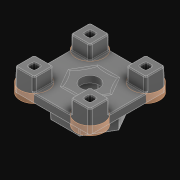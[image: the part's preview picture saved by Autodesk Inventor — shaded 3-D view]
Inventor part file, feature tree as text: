
AUTODESK INVENTOR PART (.ipt)
format: ipt  version: 2021 (Build 250183000, 183)  size: 695,808 bytes
history: native  units: in
note: dims shown in document units (in); Inventor stores cm internally (conversion verified against a paired STEP export)
features: projected_geometry x4, other x4, extrude x4, sketch x2, pattern_linear x1, fillet x1
ambient origin geometry x8: Origin, YZ Plane, XZ Plane, XY Plane, X Axis, Y Axis, Z Axis, Center Point
bodies: Solid1 (feature_tree)
feature tree (16):
  sketch  "Sketch2"  dims[d1=0.25in d2=0.25in d3=0.25in d4=0.0787in d5=0.0in d6=0.25in d7=0.25in d8=0.25in d9=0.25in d24=0.7874in d26=0.5in d27=0.7874in d29=0.5in d30=0.25in d31=0.25in]
  pattern_linear  "Rectangular Pattern1"  Spacing1=0.25in  [1 undecoded]
  sketch  "Sketch1"  dims[d0=0.25in]
  projected_geometry  "Projected Loop1"
  projected_geometry  "Projected Loop2"
  projected_geometry  "Projected Loop3"
  projected_geometry  "Projected Loop4"
  other  "Srf1"
  other  "Srf5"
  other  "Srf6"
  other  "Srf7"
  fillet  "Fillet8"  Radius=0.25in
  extrude  "ExtrusionSrf1"  Depth=0.0787in TaperAngle=0.0deg
  extrude  "ExtrusionSrf5"  Depth=0.25in
  extrude  "ExtrusionSrf6"  Depth=0.7874in
  extrude  "ExtrusionSrf7"  Depth=0.7874in
note: 1 required parameter value undecoded (feature->parameter linkage not recoverable at this tier; creation-order binding heuristic only, values carry confidence <= 0.55)
